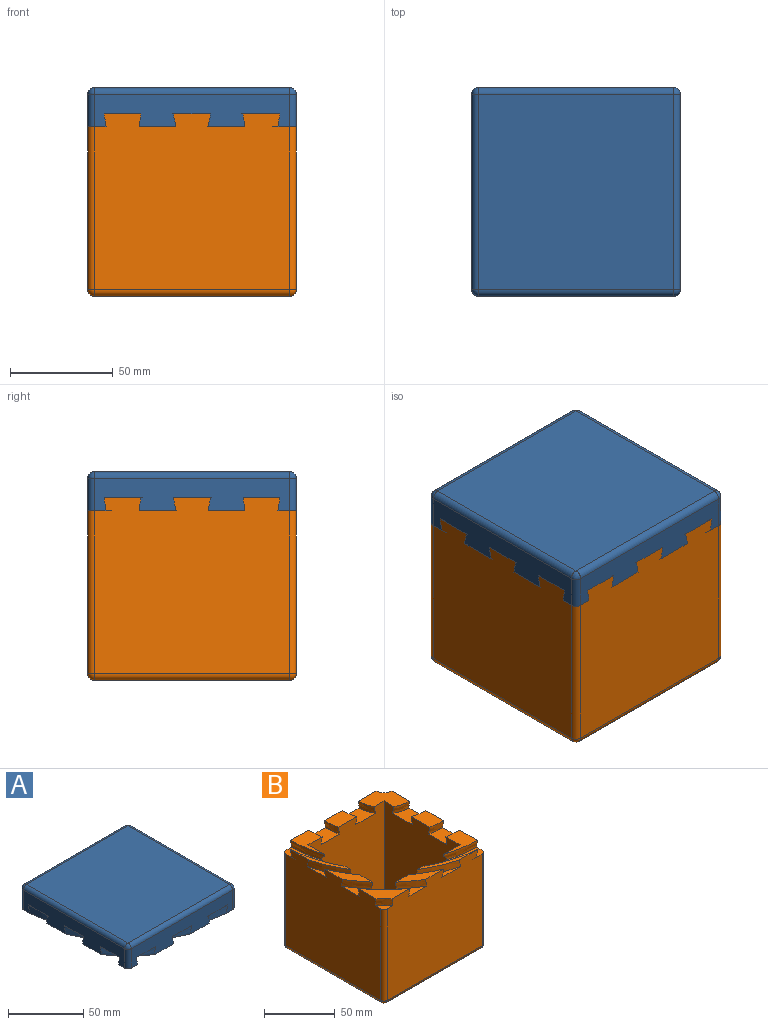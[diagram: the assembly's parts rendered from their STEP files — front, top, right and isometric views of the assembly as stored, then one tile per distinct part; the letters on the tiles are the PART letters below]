
ASSEMBLY  parts=2 mates=1
PART A: 61 faces, bbox 103.2x102.4x19.8 mm
  f0: plane 19.92x6.95mm, normal (-1,0,0), area 116.8mm2, adj f1,f2,f3,f4
  f1: plane 101.6x101.6mm, normal (0,0,-1), area 7793.1mm2, adj f0,f2,f4,f5,f6,f7,f8,f9
  f2: revolved ~13.13x6.35mm, area 85.5mm2, adj f0,f1,f3,f5
  f3: plane 21.25x12.7mm, normal (0,0,-1), area 232mm2, adj f0,f2,f4,f5
  f4: revolved ~12.96x6.35mm, area 82.9mm2, adj f0,f1,f3,f5
  f5: plane 95.25x15.88mm, normal (1,0,0), area 1189.5mm2, adj f1,f2,f3,f4,f6,f8,f9,f34
  f6: revolved ~12.88x6.35mm, area 82.3mm2, adj f1,f5,f7,f40
  f7: plane 18.7x6.94mm, normal (-1,0,0), area 109.5mm2, adj f1,f6,f8,f40
  f8: revolved ~12.84x6.35mm, area 82mm2, adj f1,f5,f7,f40
  f9: revolved ~29.15x6.35mm, area 181mm2, adj f1,f5,f10,f39
  f10: plane 24.44x7.11mm, normal (0,1,0), area 140.8mm2, adj f1,f9,f11,f39
  f11: revolved ~42.57x13.05mm, area 277.4mm2, adj f1,f10,f12,f39
  f12: plane 95.25x15.88mm, normal (0,-1,0), area 1189.5mm2, adj f1,f11,f13,f15,f16,f38,f39,f41
  f13: revolved ~30.99x12.96mm, area 207.6mm2, adj f1,f12,f14,f48
  f14: plane 10.61x6.96mm, normal (0,1,0), area 60.6mm2, adj f1,f13,f15,f48
  f15: revolved ~23.53x12.9mm, area 165.1mm2, adj f1,f12,f14,f48
  f16: revolved ~18.68x12.86mm, area 139.3mm2, adj f1,f12,f17,f47
  f17: plane 12.8x6.95mm, normal (0,1,0), area 75.4mm2, adj f1,f16,f18,f47
  f18: plane 12.86x7.01mm, normal (1,0,0), area 75.4mm2, adj f1,f17,f19,f47
  f19: revolved ~19.19x14.24mm, area 139.3mm2, adj f1,f18,f20,f47
  f20: plane 95.96x16.58mm, normal (-1,0,0), area 1189.5mm2, adj f1,f19,f21,f23,f24,f42,f43,f44
  f21: revolved ~24.3x14.02mm, area 165.1mm2, adj f1,f20,f22,f52
  f22: plane 10.67x7.01mm, normal (1,0,0), area 60.6mm2, adj f1,f21,f23,f52
  f23: revolved ~31.91x13.7mm, area 207.6mm2, adj f1,f20,f22,f52
  f24: revolved ~43.48x13.31mm, area 277.4mm2, adj f1,f20,f25,f51
  f25: plane 24.44x7.11mm, normal (1,0,0), area 140.8mm2, adj f1,f24,f26,f51
  f26: revolved ~29.15x6.35mm, area 181mm2, adj f1,f25,f27,f51
  f27: plane 95.25x15.88mm, normal (0,1,0), area 1189.5mm2, adj f1,f26,f28,f30,f31,f33,f34,f35
  f28: revolved ~12.84x6.35mm, area 82mm2, adj f1,f27,f29,f55
  f29: plane 18.7x6.94mm, normal (0,-1,0), area 109.5mm2, adj f1,f28,f30,f55
  f30: revolved ~12.88x6.35mm, area 82.3mm2, adj f1,f27,f29,f55
  f31: revolved ~12.96x6.35mm, area 82.9mm2, adj f1,f27,f32,f54
  f32: plane 19.92x6.95mm, normal (0,-1,0), area 116.8mm2, adj f1,f31,f33,f54
  f33: revolved ~13.13x6.35mm, area 85.5mm2, adj f1,f27,f32,f54
  f34: revolved ~8.89x8.89mm, area 85.5mm2, adj f1,f5,f27,f35
  f35: plane 8.89x8.89mm, normal (0,0,-1), area 59.9mm2, adj f5,f27,f34,f36
  f36: cylinder r=3.17mm len=15.88mm, axis (0,0,1), area 79.2mm2, adj f5,f27,f35,f56
  f37: cylinder r=3.17mm len=95.25mm, axis (0,-1,0), area 475mm2, adj f5,f56,f57,f58
  f38: cylinder r=3.17mm len=15.88mm, axis (0,0,-1), area 79.2mm2, adj f5,f12,f39,f57
  f39: plane 49.98x12.7mm, normal (0,0,-1), area 370.5mm2, adj f5,f9,f10,f11,f12,f38
  f40: plane 19.17x12.7mm, normal (0,0,-1), area 227.2mm2, adj f5,f6,f7,f8
  f41: cylinder r=3.17mm len=95.25mm, axis (-1,0,0), area 475mm2, adj f12,f57,f58,f59
  f42: cylinder r=3.17mm len=15.88mm, axis (0,0,1), area 79.2mm2, adj f12,f20,f43,f59
  f43: plane 8.89x8.89mm, normal (0,0,-1), area 36.1mm2, adj f12,f20,f42,f44
  f44: revolved ~9.73x8.97mm, area 76.5mm2, adj f12,f20,f43,f45
  f45: plane 25.82x25.82mm, normal (0,0,-1), area 269.7mm2, adj f12,f20,f44,f46
  f46: revolved ~26.64x26.06mm, area 229.9mm2, adj f12,f20,f45,f47
  f47: plane 42.76x42.76mm, normal (0,0,-1), area 400.2mm2, adj f12,f16,f17,f18,f19,f20,f46
  f48: plane 40.2x12.7mm, normal (0,0,-1), area 161.2mm2, adj f12,f13,f14,f15
  f49: cylinder r=3.17mm len=95.25mm, axis (0,1,0), area 475mm2, adj f20,f58,f59,f60
  f50: cylinder r=3.17mm len=15.88mm, axis (0,0,-1), area 79.2mm2, adj f20,f27,f51,f60
  f51: plane 49.98x12.7mm, normal (0,0,-1), area 370.5mm2, adj f20,f24,f25,f26,f27,f50
  f52: plane 40.2x12.7mm, normal (0,0,-1), area 161.2mm2, adj f20,f21,f22,f23
  f53: cylinder r=3.17mm len=95.25mm, axis (1,0,0), area 475mm2, adj f27,f56,f58,f60
  f54: plane 21.25x12.7mm, normal (0,0,-1), area 232mm2, adj f27,f31,f32,f33
  f55: plane 19.17x12.7mm, normal (0,0,-1), area 227.2mm2, adj f27,f28,f29,f30
  f56: sphere r=3.17mm, area 15.8mm2, adj f36,f37,f53
  f57: sphere r=3.17mm, area 15.8mm2, adj f37,f38,f41
  f58: plane 95.25x95.25mm, normal (0,0,1), area 9072.6mm2, adj f37,f41,f49,f53
  f59: sphere r=3.17mm, area 15.8mm2, adj f41,f42,f49
  f60: sphere r=3.17mm, area 15.8mm2, adj f49,f50,f53
PART B: 64 faces, bbox 103.2x102.4x89.7 mm
  f0: plane 76.8x76.8mm, normal (-1,0,0), area 5580.2mm2, adj f1,f3,f4,f10,f13,f24,f26,f28
  f1: plane 76.8x76.8mm, normal (0,-1,0), area 5580.2mm2, adj f0,f2,f4,f9,f11,f12,f15,f23
  f2: plane 76.95x76.95mm, normal (1,0,0), area 5529.6mm2, adj f1,f3,f4,f14,f15,f16,f17,f19
  f3: plane 76.95x76.95mm, normal (0,1,0), area 5529.7mm2, adj f0,f2,f4,f16,f18,f21,f36,f37
  f4: plane 76.2x76.2mm, normal (0,0,1), area 5806.4mm2, adj f0,f1,f2,f3
  f5: plane 8.89x8.89mm, normal (0,0,1), area 36.1mm2, adj f6,f49,f50,f52
  f6: revolved ~9.73x8.97mm, area 76.5mm2, adj f5,f7,f49,f50
  f7: plane 25.82x25.82mm, normal (0,0,1), area 269.7mm2, adj f6,f8,f49,f50
  f8: revolved ~26.64x26.06mm, area 229.9mm2, adj f7,f16,f49,f50
  f9: plane 19.17x12.7mm, normal (0,0,1), area 227.2mm2, adj f1,f23,f25,f48
  f10: plane 19.17x12.7mm, normal (0,0,1), area 227.2mm2, adj f0,f24,f26,f47
  f11: plane 19.75x12.7mm, normal (0,0,1), area 228.3mm2, adj f1,f25,f27,f48
  f12: plane 21.25x12.7mm, normal (0,0,1), area 232mm2, adj f1,f27,f29,f48
  f13: plane 21.25x12.7mm, normal (0,0,1), area 232mm2, adj f0,f28,f30,f47
  f14: plane 49.98x12.7mm, normal (0,0,1), area 370.5mm2, adj f2,f22,f34,f48,f49,f54
  f15: plane 29.15x18.85mm, normal (0,0,1), area 262.1mm2, adj f1,f2,f22,f23,f48
  f16: plane 42.76x42.76mm, normal (0,0,1), area 400.2mm2, adj f2,f3,f8,f31,f42,f49,f50
  f17: plane 35.44x12.7mm, normal (0,0,1), area 187.6mm2, adj f2,f31,f32,f49
  f18: plane 35.44x12.7mm, normal (0,0,1), area 187.6mm2, adj f3,f42,f43,f50
  f19: plane 40.2x12.7mm, normal (0,0,1), area 161.2mm2, adj f2,f32,f33,f49
  f20: plane 47.51x12.7mm, normal (0,0,1), area 107.1mm2, adj f2,f33,f34,f49
  f21: plane 47.51x12.7mm, normal (0,0,1), area 107.1mm2, adj f3,f45,f46,f50
  f22: revolved ~29.15x6.35mm, area 181mm2, adj f2,f14,f15,f48
  f23: revolved ~12.84x6.35mm, area 82mm2, adj f1,f9,f15,f48
  f24: revolved ~12.84x6.35mm, area 82mm2, adj f0,f10,f38,f47
  f25: revolved ~12.88x6.35mm, area 82.3mm2, adj f1,f9,f11,f48
  f26: revolved ~12.88x6.35mm, area 82.3mm2, adj f0,f10,f39,f47
  f27: revolved ~12.96x6.35mm, area 82.9mm2, adj f1,f11,f12,f48
  f28: revolved ~12.96x6.35mm, area 82.9mm2, adj f0,f13,f39,f47
  f29: revolved ~13.13x6.35mm, area 85.5mm2, adj f1,f12,f40,f48
  f30: revolved ~13.13x6.35mm, area 85.5mm2, adj f0,f13,f40,f47
  f31: revolved ~19.19x14.24mm, area 139.3mm2, adj f2,f16,f17,f49
  f32: revolved ~24.3x14.02mm, area 165.1mm2, adj f2,f17,f19,f49
  f33: revolved ~31.91x13.7mm, area 207.6mm2, adj f2,f19,f20,f49
  f34: revolved ~43.48x13.31mm, area 277.4mm2, adj f2,f14,f20,f49
  f35: plane 8.89x8.89mm, normal (0,0,1), area 59.9mm2, adj f41,f47,f48,f63
  f36: plane 49.98x12.7mm, normal (0,0,1), area 370.5mm2, adj f3,f37,f46,f47,f50,f57
  f37: revolved ~29.15x6.35mm, area 181mm2, adj f3,f36,f38,f47
  f38: plane 29.15x18.85mm, normal (0,0,1), area 262.1mm2, adj f0,f3,f24,f37,f47
  f39: plane 19.75x12.7mm, normal (0,0,1), area 228.3mm2, adj f0,f26,f28,f47
  f40: plane 25.82x25.82mm, normal (0,0,1), area 416.3mm2, adj f0,f1,f29,f30,f41,f47,f48
  f41: revolved ~8.89x8.89mm, area 85.5mm2, adj f35,f40,f47,f48
  f42: revolved ~18.68x12.86mm, area 139.3mm2, adj f3,f16,f18,f50
  f43: revolved ~23.53x12.9mm, area 165.1mm2, adj f3,f18,f44,f50
  f44: plane 40.2x12.7mm, normal (0,0,1), area 161.2mm2, adj f3,f43,f45,f50
  f45: revolved ~30.99x12.96mm, area 207.6mm2, adj f3,f21,f44,f50
  f46: revolved ~42.57x13.05mm, area 277.4mm2, adj f3,f21,f36,f50
  f47: plane 95.25x85.73mm, normal (1,0,0), area 7883mm2, adj f10,f13,f24,f26,f28,f30,f35,f36
  f48: plane 95.25x85.73mm, normal (0,1,0), area 7883mm2, adj f9,f11,f12,f14,f15,f22,f23,f25
  f49: plane 95.96x86.43mm, normal (-1,0,0), area 7883mm2, adj f5,f6,f7,f8,f14,f16,f17,f19
  f50: plane 95.25x85.73mm, normal (0,-1,0), area 7883mm2, adj f5,f6,f7,f8,f16,f18,f21,f36
  f51: plane 95.25x95.25mm, normal (0,0,-1), area 9072.6mm2, adj f55,f56,f60,f61
  f52: cylinder r=3.17mm len=79.38mm, axis (0,0,1), area 395.9mm2, adj f5,f49,f50,f53
  f53: sphere r=3.17mm, area 15.8mm2, adj f52,f55,f56
  f54: cylinder r=3.17mm len=79.38mm, axis (0,0,-1), area 395.9mm2, adj f14,f48,f49,f58
  f55: cylinder r=3.17mm len=95.25mm, axis (0,-1,0), area 475mm2, adj f49,f51,f53,f58
  f56: cylinder r=3.17mm len=95.25mm, axis (1,0,0), area 475mm2, adj f50,f51,f53,f59
  f57: cylinder r=3.17mm len=79.38mm, axis (0,0,-1), area 395.9mm2, adj f36,f47,f50,f59
  f58: sphere r=3.17mm, area 15.8mm2, adj f54,f55,f60
  f59: sphere r=3.17mm, area 15.8mm2, adj f56,f57,f61
  f60: cylinder r=3.17mm len=95.25mm, axis (-1,0,0), area 475mm2, adj f48,f51,f58,f62
  f61: cylinder r=3.17mm len=95.25mm, axis (0,1,0), area 475mm2, adj f47,f51,f59,f62
  f62: sphere r=3.17mm, area 15.8mm2, adj f60,f61,f63
  f63: cylinder r=3.17mm len=79.38mm, axis (0,0,1), area 395.9mm2, adj f35,f47,f48,f62
PLACE A t=(-0.02,-0.44,-44.43)mm
PLACE B t=(-0.02,-0.44,-44.43)mm
MATE revolute A.f1 <-> B.f40  axis (0,0,-1) through (50.78,50.36,44.47)mm
